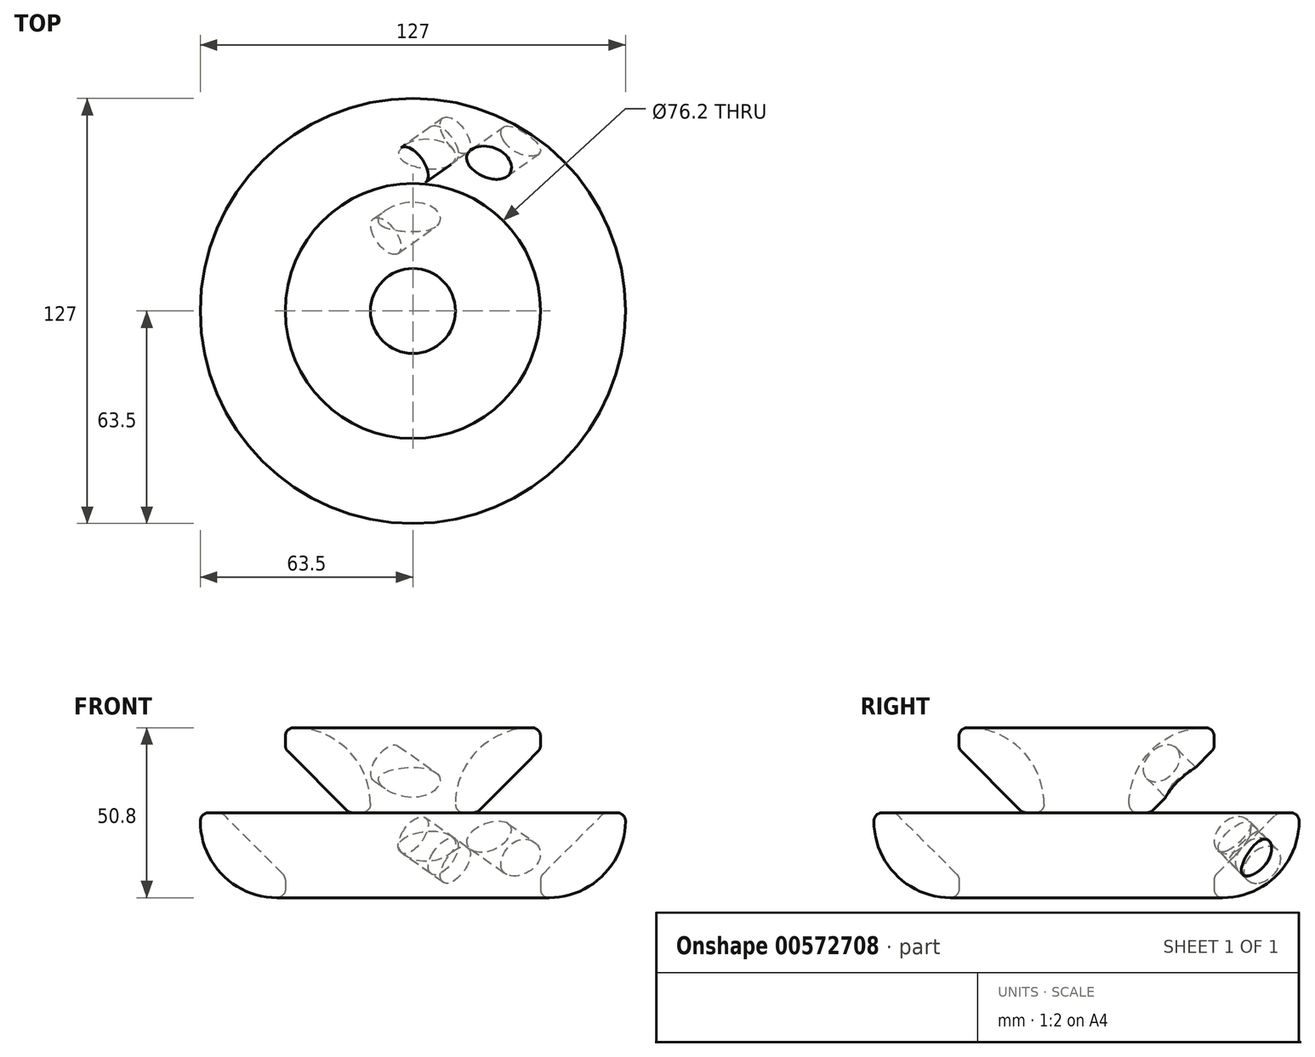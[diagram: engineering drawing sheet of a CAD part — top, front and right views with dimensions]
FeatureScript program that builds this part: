
annotation { "Feature Type Name" : "Feature", "Feature Type Description" : "" }
export const myFeature = defineFeature(function(context is Context, id is Id, definition is map)
    precondition{}
    {
        {
            var Q0;
            Q0=qCreatedBy(makeId("Top.planeOp"),FACE);
            var sketch = newSketch(context, id + "F0", { "sketchPlane" : qUnion([Q0])});
            skCircle(sketch, "E0", {"center": v(0, 0) * mm, "radius": 63.5 * mm});
            skCircle(sketch, "E1", {"center": v(0, 0) * mm, "radius": 38.1 * mm});
            skSolve(sketch);
        }
        {
            var Q0;
            Q0 = qSketchRegion(id + "F0", true);
            extrude(context, id + "F1", {"entities" : qUnion([Q0]), "depth" : 25.4 * mm, "offsetDistance" : 25.4 * mm});
        }
        {
            var Q0;
            Q0=makeQuery(id+"F1.opExtrude","CAP_EDGE",EDGE,{"disambiguationData":[OSD([sQuery(id+"F0.wireOp",EDGE,"E1")])],"isStart":false});
            chamfer(context, id + "F2", {"entities" : qUnion([Q0]), "width" : 19.05 * mm, "tangentPropagation" : true});
        }
        {
            var Q0;
            Q0=qCreatedBy(makeId("Right.planeOp"),FACE);
            var sketch = newSketch(context, id + "F3", { "sketchPlane" : qUnion([Q0])});
            skLineSegment(sketch, "E2", {"start": v(13.78, -11.24) * mm, "end": v(68.92, 43.9) * mm, "construction": true});
            skSolve(sketch);
        }
        {
            var Q0;
            Q0=sQuery(id+"F3.wireOp",EDGE,"E2");
            cPlane(context, id + "F4", {"entities" : qUnion([Q0]), "cplaneType" : CPlaneType.LINE_ANGLE, "offset" : 25.4 * mm, "angle" : 135 * degree, "width" : 152.4 * mm, "height" : 152.4 * mm});
        }
        {
            var Q0;
            Q0=qCreatedBy(id+"F4.planeOp",FACE);
            var sketch = newSketch(context, id + "F5", { "sketchPlane" : qUnion([Q0])});
            skCircle(sketch, "E3", {"center": v(43.11, 15.3) * mm, "radius": 6.35 * mm});
            skSolve(sketch);
        }
        {
            var Q0;
            Q0 = qSketchRegion(id + "F5", true);
            extrude(context, id + "F6", {"entities" : qUnion([Q0]), "operationType" : NewBodyOperationType.REMOVE, "depth" : 17.78 * mm, "offsetDistance" : 25.4 * mm});
        }
        {
            var Q0;
            Q0=qCreatedBy(makeId("Front.planeOp"),FACE);
            var sketch = newSketch(context, id + "F7", { "sketchPlane" : qUnion([Q0])});
            skLineSegment(sketch, "E4", {"start": v(0, 0) * mm, "end": v(0, 49.36) * mm, "construction": true});
            skSolve(sketch);
        }
        {
            var Q0;
            Q0=makeQuery(id+"F1.opExtrude","CAP_FACE",FACE,{"disambiguationData":[OSD([sQuery(id+"F0.wireOp",EDGE,"E0"),sQuery(id+"F0.wireOp",EDGE,"E1")])],"isStart":false});
            var sketch = newSketch(context, id + "F8", { "sketchPlane" : qUnion([Q0])});
            skCircle(sketch, "E5", {"center": v(0, 0) * mm, "radius": 38.1 * mm});
            skCircle(sketch, "E6", {"center": v(0, 0) * mm, "radius": 12.7 * mm});
            skSolve(sketch);
        }
        {
            var Q0;
            Q0 = qSketchRegion(id + "F8", true);
            extrude(context, id + "F9", {"entities" : qUnion([Q0]), "depth" : 25.4 * mm, "offsetDistance" : 25.4 * mm});
        }
        {
            var Q0;
            Q0=makeQuery(id+"F9.opExtrude","CAP_EDGE",EDGE,{"disambiguationData":[OSD([sQuery(id+"F8.wireOp",EDGE,"E5")])],"isStart":true});
            chamfer(context, id + "F10", {"entities" : qUnion([Q0]), "width" : 19.05 * mm, "tangentPropagation" : true});
        }
        {
            var Q0;
            Q0=makeQuery(id+"F1.opExtrude","CAP_EDGE",EDGE,{"disambiguationData":[OSD([sQuery(id+"F0.wireOp",EDGE,"E0")])],"isStart":true});
            fillet(context, id + "F11", {"entities" : qUnion([Q0]), "radius" : 22.86 * mm, "tangentPropagation" : true, "allowEdgeOverflow" : false});
        }
        {
            var Q0;
            Q0=makeQuery(id+"F1.opExtrude","CAP_EDGE",EDGE,{"disambiguationData":[OSD([sQuery(id+"F0.wireOp",EDGE,"E0")])],"isStart":false});
            var Q1;
            {var subQ0=sQuery(id+"F0.wireOp",EDGE,"E1");Q1=makeQuery(id+"F2.opChamfer","BLEND_EDGE",EDGE,{"blendedFrom":[makeQuery(id+"F1.opExtrude","CAP_EDGE",EDGE,{"disambiguationData":[OSD([subQ0])],"isStart":false}),makeQuery(id+"F1.opExtrude","CAP_FACE",FACE,{"disambiguationData":[OSD([sQuery(id+"F0.wireOp",EDGE,"E0"),subQ0])],"isStart":false})],"blendedInto":[makeQuery(id+"F1.opExtrude","CAP_FACE",FACE,{"disambiguationData":[OSD([sQuery(id+"F0.wireOp",EDGE,"E0"),subQ0])],"isStart":false})]});}
            var Q2;
            {var subQ0=sQuery(id+"F0.wireOp",EDGE,"E1");Q2=makeQuery(id+"F2.opChamfer","BLEND_EDGE",EDGE,{"blendedFrom":[makeQuery(id+"F1.opExtrude","CAP_EDGE",EDGE,{"disambiguationData":[OSD([subQ0])],"isStart":false}),makeQuery(id+"F1.opExtrude","SWEPT_FACE",FACE,{"disambiguationData":[OSD([subQ0])]})],"blendedInto":[makeQuery(id+"F1.opExtrude","SWEPT_FACE",FACE,{"disambiguationData":[OSD([subQ0])]})]});}
            var Q3;
            Q3=makeQuery(id+"F1.opExtrude","CAP_EDGE",EDGE,{"disambiguationData":[OSD([sQuery(id+"F0.wireOp",EDGE,"E1")])],"isStart":true});
            fillet(context, id + "F12", {"entities" : qUnion([Q0, Q1, Q2, Q3]), "radius" : 2.54 * mm, "tangentPropagation" : true, "allowEdgeOverflow" : false});
        }
        {
            var Q0;
            Q0=makeQuery(id+"F9.opExtrude","CAP_EDGE",EDGE,{"disambiguationData":[OSD([sQuery(id+"F8.wireOp",EDGE,"E6")])],"isStart":false});
            fillet(context, id + "F13", {"entities" : qUnion([Q0]), "radius" : 22.86 * mm, "tangentPropagation" : true, "allowEdgeOverflow" : false});
        }
        {
            var Q0;
            {var subQ0=sQuery(id+"F8.wireOp",EDGE,"E5");Q0=makeQuery(id+"F10.opChamfer","BLEND_EDGE",EDGE,{"blendedFrom":[makeQuery(id+"F9.opExtrude","CAP_EDGE",EDGE,{"disambiguationData":[OSD([subQ0])],"isStart":true}),makeQuery(id+"F9.opExtrude","SWEPT_FACE",FACE,{"disambiguationData":[OSD([subQ0])]})],"blendedInto":[makeQuery(id+"F9.opExtrude","SWEPT_FACE",FACE,{"disambiguationData":[OSD([subQ0])]})]});}
            var Q1;
            {var subQ0=sQuery(id+"F8.wireOp",EDGE,"E5");Q1=makeQuery(id+"F10.opChamfer","BLEND_EDGE",EDGE,{"blendedFrom":[makeQuery(id+"F9.opExtrude","CAP_EDGE",EDGE,{"disambiguationData":[OSD([subQ0])],"isStart":true}),makeQuery(id+"F9.opExtrude","CAP_FACE",FACE,{"disambiguationData":[OSD([subQ0,sQuery(id+"F8.wireOp",EDGE,"E6")])],"isStart":true})],"blendedInto":[makeQuery(id+"F9.opExtrude","CAP_FACE",FACE,{"disambiguationData":[OSD([subQ0,sQuery(id+"F8.wireOp",EDGE,"E6")])],"isStart":true})]});}
            var Q2;
            Q2=makeQuery(id+"F9.opExtrude","CAP_EDGE",EDGE,{"disambiguationData":[OSD([sQuery(id+"F8.wireOp",EDGE,"E6")])],"isStart":true});
            var Q3;
            Q3=makeQuery(id+"F9.opExtrude","CAP_EDGE",EDGE,{"disambiguationData":[OSD([sQuery(id+"F8.wireOp",EDGE,"E5")])],"isStart":false});
            fillet(context, id + "F14", {"entities" : qUnion([Q0, Q1, Q2, Q3]), "radius" : 2.54 * mm, "tangentPropagation" : true, "allowEdgeOverflow" : false});
        }
        {
            var Q0;
            Q0=qCreatedBy(makeId("Right.planeOp"),FACE);
            var sketch = newSketch(context, id + "F15", { "sketchPlane" : qUnion([Q0])});
            skLineSegment(sketch, "E7", {"start": v(19.7, 26.04) * mm, "end": v(38.74, 45.09) * mm, "construction": true});
            skSolve(sketch);
        }
        {
            var Q0;
            Q0=sQuery(id+"F15.wireOp",EDGE,"E7");
            cPlane(context, id + "F16", {"entities" : qUnion([Q0]), "cplaneType" : CPlaneType.LINE_ANGLE, "offset" : 25.4 * mm, "angle" : 135 * degree, "width" : 152.4 * mm, "height" : 152.4 * mm});
        }
        {
            var Q0;
            Q0=qCreatedBy(id+"F16.planeOp",FACE);
            var sketch = newSketch(context, id + "F17", { "sketchPlane" : qUnion([Q0])});
            skCircle(sketch, "E8", {"center": v(34.28, 28.13) * mm, "radius": 6.35 * mm});
            skSolve(sketch);
        }
        {
            var Q0;
            Q0=makeQuery(id+"F17.imprint","IMPRINT",FACE,{"disambiguationData":[TD([[makeQuery(id+"F17.imprint","IMPRINT",EDGE,{"derivedFrom":sQuery(id+"F17.wireOp",EDGE,"E8")}),1.0]])]});
            var Q1;
            Q1=sQuery(id+"F17.wireOp",EDGE,"E8");
            extrude(context, id + "F18", {"entities" : qUnion([Q0]), "operationType" : NewBodyOperationType.REMOVE, "surfaceEntities" : qUnion([Q1]), "oppositeDirection" : true, "depth" : 11.43 * mm, "offsetDistance" : 25.4 * mm, "hasSecondDirection" : true, "secondDirectionBound" : SecondDirectionBoundingType.THROUGH_ALL, "secondDirectionOppositeDirection" : false, "secondDirectionDepth" : 25.4 * mm});
        }
        {
            var Q0;
            Q0 = qSketchRegion(id + "F5", true);
            var Q1;
            Q1 = qSketchRegion(id + "F5", true);
            extrude(context, id + "F19", {"entities" : qUnion([Q0]), "surfaceEntities" : qUnion([Q1]), "depth" : 12.7 * mm, "offsetDistance" : 25.4 * mm});
        }
    });
